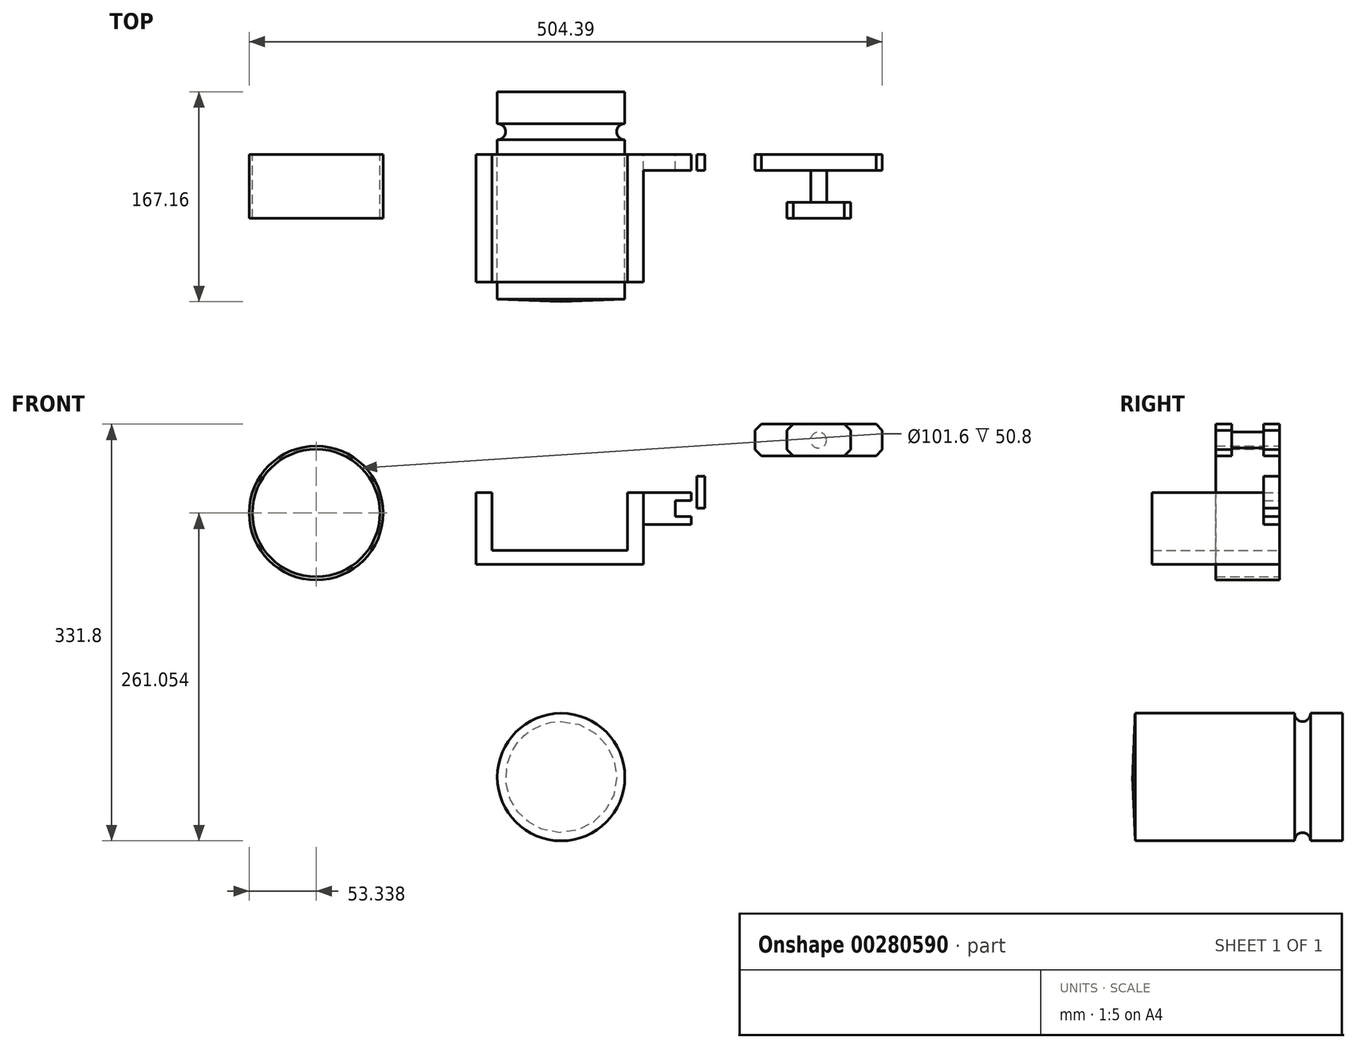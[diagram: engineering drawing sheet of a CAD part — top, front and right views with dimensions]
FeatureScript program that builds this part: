
annotation { "Feature Type Name" : "Feature", "Feature Type Description" : "" }
export const myFeature = defineFeature(function(context is Context, id is Id, definition is map)
    precondition{}
    {
        {
            var Q0;
            Q0=qCreatedBy(makeId("Front.planeOp"),FACE);
            var sketch = newSketch(context, id + "F0", { "sketchPlane" : qUnion([Q0])});
            skLineSegment(sketch, "E0", {"start": v(-55.02, -2.22) * mm, "end": v(-55.02, -48.1) * mm});
            skLineSegment(sketch, "E1", {"start": v(-55.02, -48.1) * mm, "end": v(52.93, -48.1) * mm});
            skLineSegment(sketch, "E2", {"start": v(52.93, -48.1) * mm, "end": v(52.93, -2.22) * mm});
            skLineSegment(sketch, "E3", {"start": v(52.93, -2.22) * mm, "end": v(65.63, -2.22) * mm});
            skLineSegment(sketch, "E4", {"start": v(65.63, -2.22) * mm, "end": v(65.63, -59.37) * mm});
            skLineSegment(sketch, "E5", {"start": v(65.63, -59.37) * mm, "end": v(-67.72, -59.37) * mm});
            skLineSegment(sketch, "E6", {"start": v(-67.72, -59.37) * mm, "end": v(-67.72, -2.22) * mm});
            skLineSegment(sketch, "E7", {"start": v(-67.72, -2.22) * mm, "end": v(-55.02, -2.22) * mm});
            skLineSegment(sketch, "E8", {"start": v(65.63, -2.22) * mm, "end": v(103.73, -2.22) * mm});
            skLineSegment(sketch, "E9", {"start": v(103.73, -2.22) * mm, "end": v(103.73, -8.57) * mm});
            skLineSegment(sketch, "E10", {"start": v(103.73, -8.57) * mm, "end": v(91.03, -8.57) * mm});
            skLineSegment(sketch, "E11", {"start": v(91.03, -8.57) * mm, "end": v(91.03, -21.27) * mm});
            skLineSegment(sketch, "E12", {"start": v(91.03, -21.27) * mm, "end": v(103.73, -21.27) * mm});
            skLineSegment(sketch, "E13", {"start": v(103.73, -21.27) * mm, "end": v(103.73, -27.62) * mm});
            skLineSegment(sketch, "E14", {"start": v(103.73, -27.62) * mm, "end": v(65.63, -27.62) * mm});
            skSolve(sketch);
        }
        {
            var Q0;
            Q0=makeQuery(id+"F0.imprint","IMPRINT",FACE,{"disambiguationData":[TD([[makeQuery(id+"F0.imprint","IMPRINT",EDGE,{"derivedFrom":sQuery(id+"F0.wireOp",EDGE,"E0")}),-1.0]])]});
            extrude(context, id + "F1", {"entities" : qUnion([Q0]), "depth" : 101.6 * mm});
        }
        {
            var Q0;
            Q0=qCreatedBy(makeId("Front.planeOp"),FACE);
            var sketch = newSketch(context, id + "F2", { "sketchPlane" : qUnion([Q0])});
            skCircle(sketch, "E15", {"center": v(-195.12, -18.35) * mm, "radius": 50.8 * mm});
            skCircle(sketch, "E16", {"center": v(-195.12, -18.35) * mm, "radius": 53.34 * mm});
            skSolve(sketch);
        }
        {
            var Q0;
            Q0 = qSketchRegion(id + "F2", true);
            extrude(context, id + "F3", {"entities" : qUnion([Q0]), "depth" : 50.8 * mm});
        }
        {
            var Q0;
            Q0=qCreatedBy(makeId("Front.planeOp"),FACE);
            var sketch = newSketch(context, id + "F4", { "sketchPlane" : qUnion([Q0])});
            skLineSegment(sketch, "E17.bottom", {"start": v(154.33, 52.4) * mm, "end": v(255.93, 52.4) * mm});
            skLineSegment(sketch, "E17.top", {"start": v(154.33, 27) * mm, "end": v(255.93, 27) * mm});
            skLineSegment(sketch, "E17.left", {"start": v(154.33, 52.4) * mm, "end": v(154.33, 27) * mm});
            skLineSegment(sketch, "E17.right", {"start": v(255.93, 52.4) * mm, "end": v(255.93, 27) * mm});
            skSolve(sketch);
        }
        {
            var Q0;
            Q0 = qSketchRegion(id + "F4", true);
            extrude(context, id + "F5", {"entities" : qUnion([Q0]), "depth" : 12.7 * mm});
        }
        {
            var Q0;
            Q0=makeQuery(id+"F5.opExtrude","CAP_FACE",FACE,{"disambiguationData":[OSD([sQuery(id+"F4.wireOp",EDGE,"E17.bottom"),sQuery(id+"F4.wireOp",EDGE,"E17.top"),sQuery(id+"F4.wireOp",EDGE,"E17.left"),sQuery(id+"F4.wireOp",EDGE,"E17.right")])],"isStart":false});
            var sketch = newSketch(context, id + "F6", { "sketchPlane" : qUnion([Q0])});
            skCircle(sketch, "E18", {"center": v(205.13, 39.7) * mm, "radius": 6.35 * mm});
            skSolve(sketch);
        }
        {
            var Q0;
            Q0 = qSketchRegion(id + "F6", true);
            extrude(context, id + "F7", {"entities" : qUnion([Q0]), "operationType" : NewBodyOperationType.ADD, "depth" : 25.4 * mm});
        }
        {
            var Q0;
            Q0=makeQuery(id+"F7.opExtrude","CAP_FACE",FACE,{"disambiguationData":[OSD([sQuery(id+"F6.wireOp",EDGE,"E18")])],"isStart":false});
            var sketch = newSketch(context, id + "F8", { "sketchPlane" : qUnion([Q0])});
            skLineSegment(sketch, "E19.bottom", {"start": v(179.73, 27) * mm, "end": v(230.53, 27) * mm});
            skLineSegment(sketch, "E19.top", {"start": v(179.73, 52.4) * mm, "end": v(230.53, 52.4) * mm});
            skLineSegment(sketch, "E19.left", {"start": v(179.73, 27) * mm, "end": v(179.73, 52.4) * mm});
            skLineSegment(sketch, "E19.right", {"start": v(230.53, 27) * mm, "end": v(230.53, 52.4) * mm});
            skPoint(sketch, "E19.middle", {"position": v(205.13, 39.7) * mm});
            skSolve(sketch);
        }
        {
            var Q0;
            Q0 = qSketchRegion(id + "F8", true);
            extrude(context, id + "F9", {"entities" : qUnion([Q0]), "operationType" : NewBodyOperationType.ADD, "depth" : 12.7 * mm});
        }
        {
            var Q0;
            Q0=makeQuery(id+"F5.opExtrude","SWEPT_EDGE",EDGE,{"disambiguationData":[OSD([sQuery(id+"F4.wireOp",EDGE,"E17.bottom"),sQuery(id+"F4.wireOp",EDGE,"E17.left")])]});
            var Q1;
            Q1=makeQuery(id+"F5.opExtrude","SWEPT_EDGE",EDGE,{"disambiguationData":[OSD([sQuery(id+"F4.wireOp",EDGE,"E17.top"),sQuery(id+"F4.wireOp",EDGE,"E17.left")])]});
            var Q2;
            Q2=makeQuery(id+"F9.opExtrude","SWEPT_EDGE",EDGE,{"disambiguationData":[OSD([sQuery(id+"F8.wireOp",EDGE,"E19.bottom"),sQuery(id+"F8.wireOp",EDGE,"E19.left")])]});
            var Q3;
            Q3=makeQuery(id+"F9.opExtrude","SWEPT_EDGE",EDGE,{"disambiguationData":[OSD([sQuery(id+"F8.wireOp",EDGE,"E19.top"),sQuery(id+"F8.wireOp",EDGE,"E19.left")])]});
            var Q4;
            Q4=makeQuery(id+"F9.opExtrude","SWEPT_EDGE",EDGE,{"disambiguationData":[OSD([sQuery(id+"F8.wireOp",EDGE,"E19.top"),sQuery(id+"F8.wireOp",EDGE,"E19.right")])]});
            var Q5;
            Q5=makeQuery(id+"F5.opExtrude","SWEPT_EDGE",EDGE,{"disambiguationData":[OSD([sQuery(id+"F4.wireOp",EDGE,"E17.bottom"),sQuery(id+"F4.wireOp",EDGE,"E17.right")])]});
            var Q6;
            Q6=makeQuery(id+"F5.opExtrude","SWEPT_EDGE",EDGE,{"disambiguationData":[OSD([sQuery(id+"F4.wireOp",EDGE,"E17.top"),sQuery(id+"F4.wireOp",EDGE,"E17.right")])]});
            var Q7;
            Q7=makeQuery(id+"F9.opExtrude","SWEPT_EDGE",EDGE,{"disambiguationData":[OSD([sQuery(id+"F8.wireOp",EDGE,"E19.bottom"),sQuery(id+"F8.wireOp",EDGE,"E19.right")])]});
            var Q8;
            Q8=makeQuery(id+"F7.opExtrude","CAP_EDGE",EDGE,{"disambiguationData":[OSD([sQuery(id+"F6.wireOp",EDGE,"E18")])],"isStart":true});
            var Q9;
            Q9=makeQuery(id+"F7.opExtrude","CAP_EDGE",EDGE,{"disambiguationData":[OSD([sQuery(id+"F6.wireOp",EDGE,"E18")])],"isStart":false});
            chamfer(context, id + "F10", {"entities" : qUnion([Q0, Q1, Q2, Q3, Q4, Q5, Q6, Q7, Q8, Q9]), "width" : 5.08 * mm, "tangentPropagation" : true});
        }
        {
            var Q0;
            {var subQ0=sQuery(id+"F0.wireOp",EDGE,"E8");Q0=makeQuery(id+"F0.imprint","IMPRINT",FACE,{"disambiguationData":[TD([[makeQuery(id+"F0.imprint","IMPRINT",EDGE,{"derivedFrom":subQ0}),-1.0]])]});}
            extrude(context, id + "F11", {"entities" : qUnion([Q0]), "operationType" : NewBodyOperationType.ADD, "depth" : 12.7 * mm});
        }
        {
            var Q0;
            Q0=qCreatedBy(makeId("Front.planeOp"),FACE);
            var sketch = newSketch(context, id + "F12", { "sketchPlane" : qUnion([Q0])});
            skLineSegment(sketch, "E20.bottom", {"start": v(114.41, -14.6) * mm, "end": v(108.06, -14.6) * mm});
            skLineSegment(sketch, "E20.top", {"start": v(114.41, 10.8) * mm, "end": v(108.06, 10.8) * mm});
            skLineSegment(sketch, "E20.left", {"start": v(114.41, -14.6) * mm, "end": v(114.41, 10.8) * mm});
            skLineSegment(sketch, "E20.right", {"start": v(108.06, -14.6) * mm, "end": v(108.06, 10.8) * mm});
            skPoint(sketch, "E20.middle", {"position": v(111.24, -1.9) * mm});
            skSolve(sketch);
        }
        {
            var Q0;
            Q0 = qSketchRegion(id + "F12", true);
            extrude(context, id + "F13", {"entities" : qUnion([Q0]), "depth" : 12.7 * mm});
        }
        {
            var Q0;
            Q0=qCreatedBy(makeId("Right.planeOp"),FACE);
            var sketch = newSketch(context, id + "F14", { "sketchPlane" : qUnion([Q0])});
            skLineSegment(sketch, "E21", {"start": v(-115.03, -279.4) * mm, "end": v(11.97, -279.4) * mm});
            skArc(sketch, "E22", {"start": v(24.67, -279.4) * mm, "mid": v(18.32, -272.83) * mm, "end": v(11.97, -279.4) * mm});
            skLineSegment(sketch, "E23", {"start": v(24.67, -279.4) * mm, "end": v(50.07, -279.4) * mm});
            skLineSegment(sketch, "E24", {"start": v(50.07, -279.4) * mm, "end": v(50.07, -228.6) * mm});
            skLineSegment(sketch, "E25", {"start": v(50.07, -228.6) * mm, "end": v(-117.1, -228.6) * mm});
            skLineSegment(sketch, "E26", {"start": v(-117.1, -228.6) * mm, "end": v(-115.03, -279.4) * mm});
            skSolve(sketch);
        }
        {
            var Q0;
            Q0 = qSketchRegion(id + "F14", true);
            var Q1;
            Q1=sQuery(id+"F14.wireOp",EDGE,"E25");
            revolve(context, id + "F15", {"entities" : qUnion([Q0]), "axis" : qUnion([Q1]), "revolveType" : RevolveType.FULL});
        }
    });
